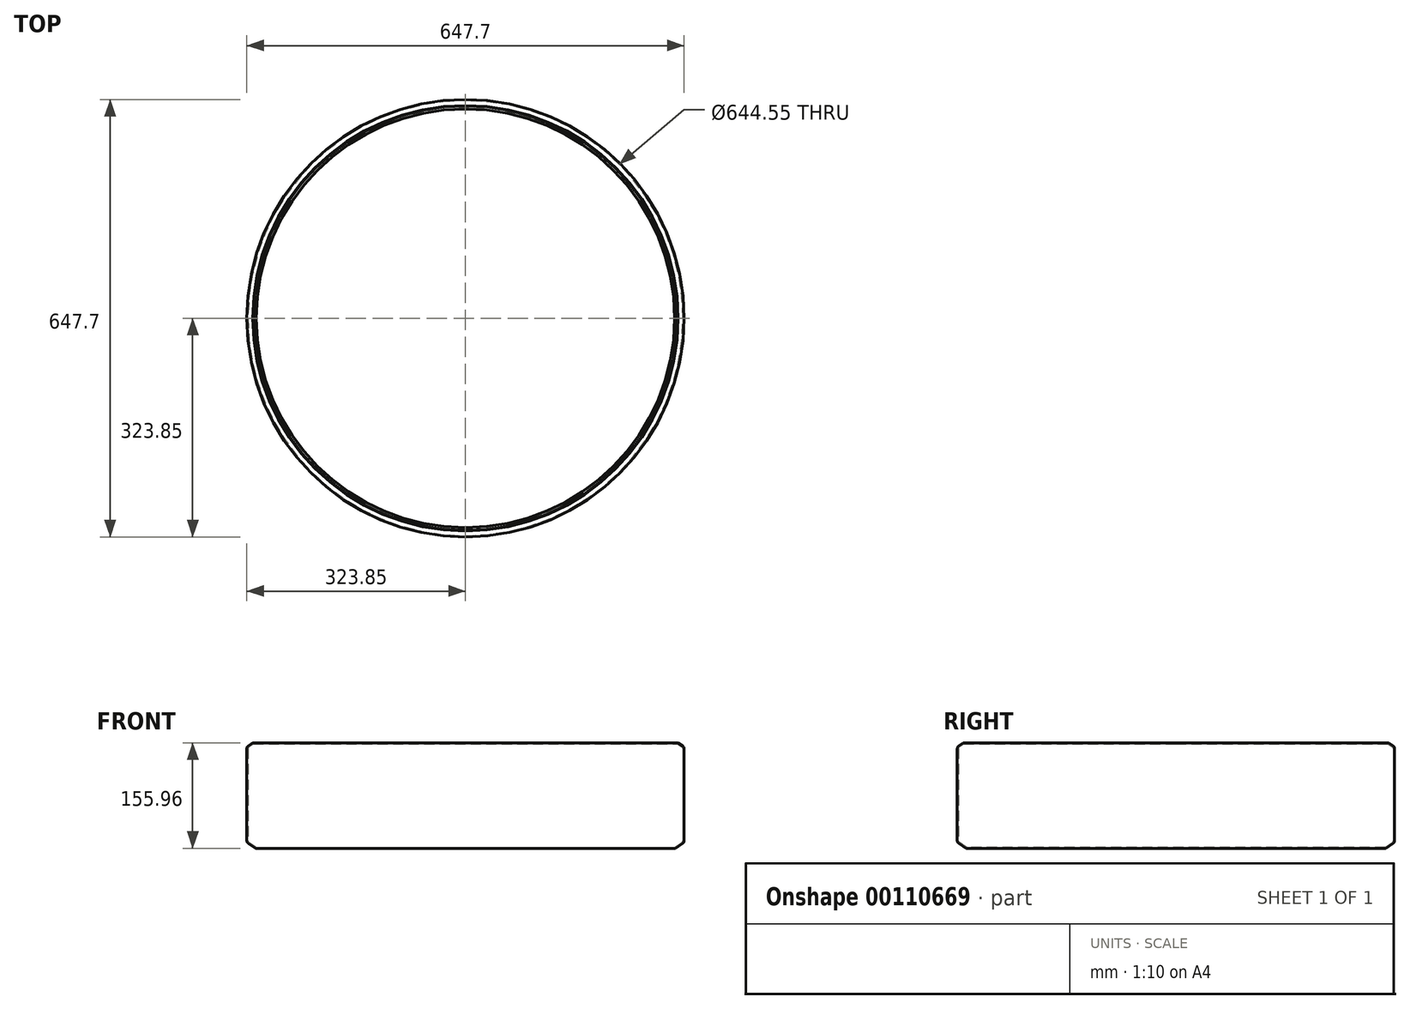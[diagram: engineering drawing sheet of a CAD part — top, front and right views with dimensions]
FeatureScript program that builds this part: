
annotation { "Feature Type Name" : "Feature", "Feature Type Description" : "" }
export const myFeature = defineFeature(function(context is Context, id is Id, definition is map)
    precondition{}
    {
        {
            var Q0;
            Q0=qCreatedBy(makeId("Front.planeOp"),FACE);
            var sketch = newSketch(context, id + "F0", { "sketchPlane" : qUnion([Q0])});
            skLineSegment(sketch, "E0", {"start": v(-322.28, -5.1) * mm, "end": v(-322.28, 63.05) * mm});
            skLineSegment(sketch, "E1", {"start": v(-320.86, 65.69) * mm, "end": v(-314.16, 70.15) * mm});
            skLineSegment(sketch, "E2", {"start": v(-322.28, -5.1) * mm, "end": v(-322.28, -73.26) * mm});
            skLineSegment(sketch, "E3", {"start": v(-320.86, -75.9) * mm, "end": v(-309.92, -83.2) * mm});
            skLineSegment(sketch, "E4.0", {"start": v(-321.73, -77.21) * mm, "end": v(-310.8, -84.5) * mm});
            skLineSegment(sketch, "E4.1", {"start": v(-323.85, 0) * mm, "end": v(-323.85, -73.25) * mm});
            skLineSegment(sketch, "E4.2", {"start": v(-323.85, 0) * mm, "end": v(-323.85, 63.04) * mm});
            skLineSegment(sketch, "E4.3", {"start": v(-321.73, 67) * mm, "end": v(-315.04, 71.46) * mm});
            skLineSegment(sketch, "E5", {"start": v(-315.04, 71.46) * mm, "end": v(-314.16, 70.15) * mm});
            skLineSegment(sketch, "E6", {"start": v(-309.92, -83.2) * mm, "end": v(-310.8, -84.5) * mm});
            skPoint(sketch, "E7.visualSharp", {"position": v(-322.28, 64.75) * mm});
            skArc(sketch, "E7.filletArc", {"start": v(-320.86, 65.69) * mm, "mid": v(-321.9, 64.54) * mm, "end": v(-322.28, 63.05) * mm});
            skPoint(sketch, "E8.visualSharp", {"position": v(-322.28, -74.95) * mm});
            skArc(sketch, "E8.filletArc", {"start": v(-322.28, -73.26) * mm, "mid": v(-321.9, -74.75) * mm, "end": v(-320.86, -75.9) * mm});
            skPoint(sketch, "E9.visualSharp", {"position": v(-323.85, -75.8) * mm});
            skArc(sketch, "E9.filletArc", {"start": v(-323.85, -73.25) * mm, "mid": v(-323.29, -75.5) * mm, "end": v(-321.73, -77.21) * mm});
            skPoint(sketch, "E10.visualSharp", {"position": v(-323.85, 65.59) * mm});
            skArc(sketch, "E10.filletArc", {"start": v(-321.73, 67) * mm, "mid": v(-323.29, 65.29) * mm, "end": v(-323.85, 63.04) * mm});
            skSolve(sketch);
        }
        {
            var Q0;
            Q0=qCreatedBy(makeId("Front.planeOp"),FACE);
            var sketch = newSketch(context, id + "F1", { "sketchPlane" : qUnion([Q0])});
            skLineSegment(sketch, "E11", {"start": v(0, 0) * mm, "end": v(0, 91.97) * mm});
            skSolve(sketch);
        }
        {
            var Q0;
            Q0 = qSketchRegion(id + "F0", true);
            var Q1;
            Q1=sQuery(id+"F1.wireOp",EDGE,"E11");
            revolve(context, id + "F2", {"entities" : qUnion([Q0]), "axis" : qUnion([Q1]), "revolveType" : RevolveType.FULL});
        }
    });
